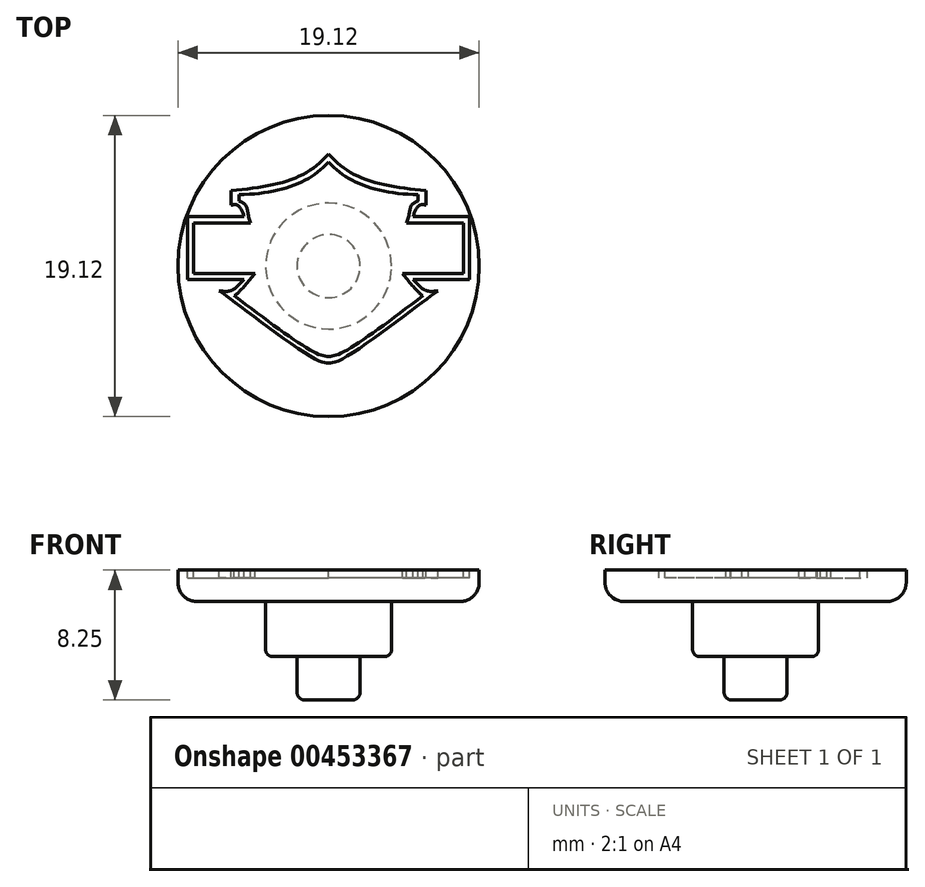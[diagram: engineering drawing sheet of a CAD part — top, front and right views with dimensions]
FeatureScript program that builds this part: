
annotation { "Feature Type Name" : "Feature", "Feature Type Description" : "" }
export const myFeature = defineFeature(function(context is Context, id is Id, definition is map)
    precondition{}
    {
        {
            var Q0;
            Q0=qCreatedBy(makeId("Top.planeOp"),FACE);
            var sketch = newSketch(context, id + "F0", { "sketchPlane" : qUnion([Q0])});
            skCircle(sketch, "E0", {"center": v(0, 0) * mm, "radius": 9.56 * mm});
            skSolve(sketch);
        }
        {
            var Q0;
            Q0=makeQuery(id+"F0.imprint","IMPRINT",FACE,{"disambiguationData":[TD([[makeQuery(id+"F0.imprint","IMPRINT",EDGE,{"derivedFrom":sQuery(id+"F0.wireOp",EDGE,"E0")}),1.0]])]});
            extrude(context, id + "F1", {"entities" : qUnion([Q0]), "depth" : 2 * mm, "offsetDistance" : 25 * mm});
        }
        {
            var Q0;
            Q0=makeQuery(id+"F1.opExtrude","CAP_FACE",FACE,{"disambiguationData":[OSD([sQuery(id+"F0.wireOp",EDGE,"E0")])],"isStart":false});
            var sketch = newSketch(context, id + "F2", { "sketchPlane" : qUnion([Q0])});
            skLineSegment(sketch, "E1", {"start": v(-8.96, 3.14) * mm, "end": v(-8.96, -0.86) * mm});
            skLineSegment(sketch, "E2", {"start": v(-8.96, -0.86) * mm, "end": v(-5.36, -0.86) * mm});
            skLineSegment(sketch, "E3", {"start": v(-8.96, 3.14) * mm, "end": v(-5.36, 3.14) * mm});
            skLineSegment(sketch, "E4", {"start": v(-6.2, 3.86) * mm, "end": v(-6.2, 4.8) * mm});
            skFitSpline(sketch, "E5", {"points": [v(-6.2, 4.8) * mm, v(-2.2, 5.56) * mm, v(0, 7.11) * mm], "startDerivative": vector(8, 0.7) * mm, "endDerivative": vector(4.22, 4.69) * mm});
            skPoint(sketch, "E6.1.internal.snap0", {"position": v(-5.76, 3.46) * mm});
            skFitSpline(sketch, "E6", {"points": [v(-6.2, 3.86) * mm, v(-5.76, 3.86) * mm, v(-5.36, 3.14) * mm], "startDerivative": vector(1.06, 0.27) * mm, "endDerivative": vector(0.57, -1.73) * mm});
            skPoint(sketch, "E7.1.internal.snap0", {"position": v(-6.16, -1.25) * mm});
            skFitSpline(sketch, "E7", {"points": [v(-5.36, -0.86) * mm, v(-6.16, -1.55) * mm, v(-6.96, -1.57) * mm], "startDerivative": vector(-1.46, -1.45) * mm, "endDerivative": vector(-1.74, 0.21) * mm});
            skFitSpline(sketch, "E8", {"points": [v(-6.96, -1.57) * mm, v(-6.37, -2) * mm, v(-0.83, -5.91) * mm, v(0, -6.14) * mm], "startDerivative": vector(1.87, -1.24) * mm, "endDerivative": vector(2.74, 0.01) * mm});
            skFitSpline(sketch, "E9.MirrorCS", {"points": [v(6.2, 4.8) * mm, v(2.2, 5.56) * mm, v(0, 7.11) * mm], "startDerivative": vector(-8, 0.7) * mm, "endDerivative": vector(-4.22, 4.69) * mm});
            skLineSegment(sketch, "E10.MirrorCS", {"start": v(6.2, 3.86) * mm, "end": v(6.2, 4.8) * mm});
            skFitSpline(sketch, "E11.MirrorCS", {"points": [v(6.2, 3.86) * mm, v(5.76, 3.86) * mm, v(5.36, 3.14) * mm], "startDerivative": vector(-1.06, 0.27) * mm, "endDerivative": vector(-0.57, -1.73) * mm});
            skLineSegment(sketch, "E12.MirrorCS", {"start": v(8.96, 3.14) * mm, "end": v(5.36, 3.14) * mm});
            skLineSegment(sketch, "E13.MirrorCS", {"start": v(8.96, 3.14) * mm, "end": v(8.96, -0.86) * mm});
            skLineSegment(sketch, "E14.MirrorCS", {"start": v(8.96, -0.86) * mm, "end": v(5.36, -0.86) * mm});
            skFitSpline(sketch, "E15.MirrorCS", {"points": [v(5.36, -0.86) * mm, v(6.16, -1.55) * mm, v(6.96, -1.57) * mm], "startDerivative": vector(1.46, -1.45) * mm, "endDerivative": vector(1.74, 0.21) * mm});
            skFitSpline(sketch, "E16.MirrorCS", {"points": [v(6.96, -1.57) * mm, v(6.37, -2) * mm, v(0.83, -5.91) * mm, v(0, -6.14) * mm], "startDerivative": vector(-1.87, -1.24) * mm, "endDerivative": vector(-2.74, 0.01) * mm});
            skLineSegment(sketch, "E17", {"start": v(-8.56, 2.74) * mm, "end": v(-8.56, -0.46) * mm});
            skLineSegment(sketch, "E18", {"start": v(-8.56, -0.46) * mm, "end": v(-4.68, -0.46) * mm});
            skLineSegment(sketch, "E19", {"start": v(-8.56, 2.74) * mm, "end": v(-4.95, 2.74) * mm});
            skLineSegment(sketch, "E20", {"start": v(-5.7, 4.54) * mm, "end": v(-5.7, 4.12) * mm});
            skFitSpline(sketch, "E21", {"points": [v(-4.95, 2.74) * mm, v(-5.26, 3.86) * mm, v(-5.7, 4.12) * mm], "startDerivative": vector(-0.98, 2.31) * mm, "endDerivative": vector(-1.34, 0.39) * mm});
            skFitSpline(sketch, "E22", {"points": [v(-5.7, 4.54) * mm, v(-2.02, 5.2) * mm, v(0, 6.61) * mm], "startDerivative": vector(7.72, 0.09) * mm, "endDerivative": vector(3.8, 4.12) * mm});
            skFitSpline(sketch, "E23", {"points": [v(-4.68, -0.46) * mm, v(-5.87, -1.82) * mm, v(-6, -1.88) * mm], "startDerivative": vector(-1.78, -2.38) * mm, "endDerivative": vector(-0.7, 0.2) * mm});
            skFitSpline(sketch, "E24", {"points": [v(-6, -1.88) * mm, v(-0.83, -5.51) * mm, v(0, -5.74) * mm], "startDerivative": vector(8.55, -6.43) * mm, "endDerivative": vector(2.54, -0.24) * mm});
            skFitSpline(sketch, "E25.MirrorCS", {"points": [v(5.7, 4.54) * mm, v(2.02, 5.2) * mm, v(0, 6.61) * mm], "startDerivative": vector(-7.72, 0.09) * mm, "endDerivative": vector(-3.8, 4.12) * mm});
            skLineSegment(sketch, "E26.MirrorCS", {"start": v(5.7, 4.54) * mm, "end": v(5.7, 4.12) * mm});
            skFitSpline(sketch, "E27.MirrorCS", {"points": [v(4.95, 2.74) * mm, v(5.26, 3.86) * mm, v(5.7, 4.12) * mm], "startDerivative": vector(0.98, 2.31) * mm, "endDerivative": vector(1.34, 0.39) * mm});
            skLineSegment(sketch, "E28.MirrorCS", {"start": v(8.56, 2.74) * mm, "end": v(4.95, 2.74) * mm});
            skLineSegment(sketch, "E29.MirrorCS", {"start": v(8.56, 2.74) * mm, "end": v(8.56, -0.46) * mm});
            skLineSegment(sketch, "E30.MirrorCS", {"start": v(8.56, -0.46) * mm, "end": v(4.68, -0.46) * mm});
            skFitSpline(sketch, "E31.MirrorCS", {"points": [v(4.68, -0.46) * mm, v(5.87, -1.82) * mm, v(6, -1.88) * mm], "startDerivative": vector(1.78, -2.38) * mm, "endDerivative": vector(0.7, 0.2) * mm});
            skFitSpline(sketch, "E32.MirrorCS", {"points": [v(6, -1.88) * mm, v(0.83, -5.51) * mm, v(0, -5.74) * mm], "startDerivative": vector(-8.55, -6.43) * mm, "endDerivative": vector(-2.54, -0.24) * mm});
            skLineSegment(sketch, "E33", {"start": v(2.15, -2.68) * mm, "end": v(2.15, -1.58) * mm});
            skLineSegment(sketch, "E34", {"start": v(2.15, -1.58) * mm, "end": v(3.17, -1.58) * mm});
            skLineSegment(sketch, "E35", {"start": v(3.17, -1.58) * mm, "end": v(4.17, -0.45) * mm});
            skLineSegment(sketch, "E36", {"start": v(4.17, -0.45) * mm, "end": v(3.5, 1.2) * mm});
            skLineSegment(sketch, "E37", {"start": v(3.5, 1.2) * mm, "end": v(3.87, 1.77) * mm});
            skLineSegment(sketch, "E38", {"start": v(0, -0.93) * mm, "end": v(0.17, -1.7) * mm});
            skLineSegment(sketch, "E39", {"start": v(0.17, -1.7) * mm, "end": v(0.88, -1.7) * mm});
            skLineSegment(sketch, "E40", {"start": v(0.88, -1.7) * mm, "end": v(0.17, -0.56) * mm});
            skLineSegment(sketch, "E41", {"start": v(0.17, -0.56) * mm, "end": v(1.4, -1.08) * mm});
            skLineSegment(sketch, "E42", {"start": v(1.4, -1.08) * mm, "end": v(2.63, -0.22) * mm});
            skLineSegment(sketch, "E43", {"start": v(2.63, -0.22) * mm, "end": v(1.88, 0.38) * mm});
            skLineSegment(sketch, "E44", {"start": v(1.88, 0.38) * mm, "end": v(0.17, 0) * mm});
            skLineSegment(sketch, "E45", {"start": v(0.17, 0) * mm, "end": v(-1.23, -1.7) * mm});
            skLineSegment(sketch, "E46", {"start": v(-1.23, -1.7) * mm, "end": v(-0.37, -1.7) * mm});
            skLineSegment(sketch, "E47", {"start": v(-0.37, -1.7) * mm, "end": v(0, -0.93) * mm});
            skLineSegment(sketch, "E48.MirrorCS", {"start": v(-1.88, 0.38) * mm, "end": v(-0.17, 0) * mm});
            skLineSegment(sketch, "E49.MirrorCS", {"start": v(-2.63, -0.22) * mm, "end": v(-1.88, 0.38) * mm});
            skLineSegment(sketch, "E50.MirrorCS", {"start": v(-1.4, -1.08) * mm, "end": v(-2.63, -0.22) * mm});
            skLineSegment(sketch, "E51.MirrorCS", {"start": v(-0.17, -0.56) * mm, "end": v(-1.4, -1.08) * mm});
            skLineSegment(sketch, "E52.MirrorCS", {"start": v(-4.17, -0.45) * mm, "end": v(-3.5, 1.2) * mm});
            skLineSegment(sketch, "E53.MirrorCS", {"start": v(-3.17, -1.58) * mm, "end": v(-4.17, -0.45) * mm});
            skLineSegment(sketch, "E54.MirrorCS", {"start": v(-2.15, -1.58) * mm, "end": v(-3.17, -1.58) * mm});
            skLineSegment(sketch, "E55.MirrorCS", {"start": v(-2.15, -2.68) * mm, "end": v(-2.15, -1.58) * mm});
            skLineSegment(sketch, "E56.MirrorCS", {"start": v(-3.5, 1.2) * mm, "end": v(-3.87, 1.77) * mm});
            skLineSegment(sketch, "E57", {"start": v(-2.15, -2.68) * mm, "end": v(2.15, -2.68) * mm});
            skSolve(sketch);
        }
        {
            var Q0;
            Q0 = qSketchRegion(id + "F2", true);
            extrude(context, id + "F3", {"entities" : qUnion([Q0]), "operationType" : NewBodyOperationType.REMOVE, "oppositeDirection" : true, "depth" : .5 * mm, "offsetDistance" : 25 * mm});
        }
        {
            var Q0;
            Q0=makeQuery(id+"F1.opExtrude","CAP_FACE",FACE,{"disambiguationData":[OSD([sQuery(id+"F0.wireOp",EDGE,"E0")])],"isStart":true});
            var sketch = newSketch(context, id + "F4", { "sketchPlane" : qUnion([Q0])});
            skCircle(sketch, "E58", {"center": v(0, 0) * mm, "radius": 4 * mm});
            skSolve(sketch);
        }
        {
            var Q0;
            Q0=makeQuery(id+"F4.imprint","IMPRINT",FACE,{"disambiguationData":[TD([[makeQuery(id+"F4.imprint","IMPRINT",EDGE,{"derivedFrom":sQuery(id+"F4.wireOp",EDGE,"E58")}),1.0]])]});
            extrude(context, id + "F5", {"entities" : qUnion([Q0]), "operationType" : NewBodyOperationType.ADD, "depth" : 3.5 * mm, "offsetDistance" : 25 * mm});
        }
        {
            var Q0;
            Q0=makeQuery(id+"F1.opExtrude","CAP_EDGE",EDGE,{"disambiguationData":[OSD([sQuery(id+"F0.wireOp",EDGE,"E0")])],"isStart":true});
            fillet(context, id + "F6", {"entities" : qUnion([Q0]), "radius" : 1.2 * mm, "tangentPropagation" : true, "allowEdgeOverflow" : false});
        }
        {
            var Q0;
            Q0=makeQuery(id+"F5.opExtrude","CAP_FACE",FACE,{"disambiguationData":[OSD([sQuery(id+"F4.wireOp",EDGE,"E58")])],"isStart":false});
            var sketch = newSketch(context, id + "F7", { "sketchPlane" : qUnion([Q0])});
            skCircle(sketch, "E59", {"center": v(0, 0) * mm, "radius": 2 * mm});
            skSolve(sketch);
        }
        {
            var Q0;
            Q0=makeQuery(id+"F7.imprint","IMPRINT",FACE,{"disambiguationData":[TD([[makeQuery(id+"F7.imprint","IMPRINT",EDGE,{"derivedFrom":sQuery(id+"F7.wireOp",EDGE,"E59")}),1.0]])]});
            extrude(context, id + "F8", {"entities" : qUnion([Q0]), "operationType" : NewBodyOperationType.ADD, "depth" : 2.75 * mm, "offsetDistance" : 25 * mm});
        }
        {
            var Q0;
            Q0=makeQuery(id+"F8.opExtrude","CAP_EDGE",EDGE,{"disambiguationData":[OSD([sQuery(id+"F7.wireOp",EDGE,"E59")])],"isStart":false});
            fillet(context, id + "F9", {"entities" : qUnion([Q0]), "radius" : 0.48 * mm, "tangentPropagation" : true, "allowEdgeOverflow" : false});
        }
        {
            var Q0;
            Q0=makeQuery(id+"F5.opExtrude","CAP_EDGE",EDGE,{"disambiguationData":[OSD([sQuery(id+"F4.wireOp",EDGE,"E58")])],"isStart":false});
            fillet(context, id + "F10", {"entities" : qUnion([Q0]), "radius" : 0.46 * mm, "tangentPropagation" : true, "allowEdgeOverflow" : false});
        }
    });
